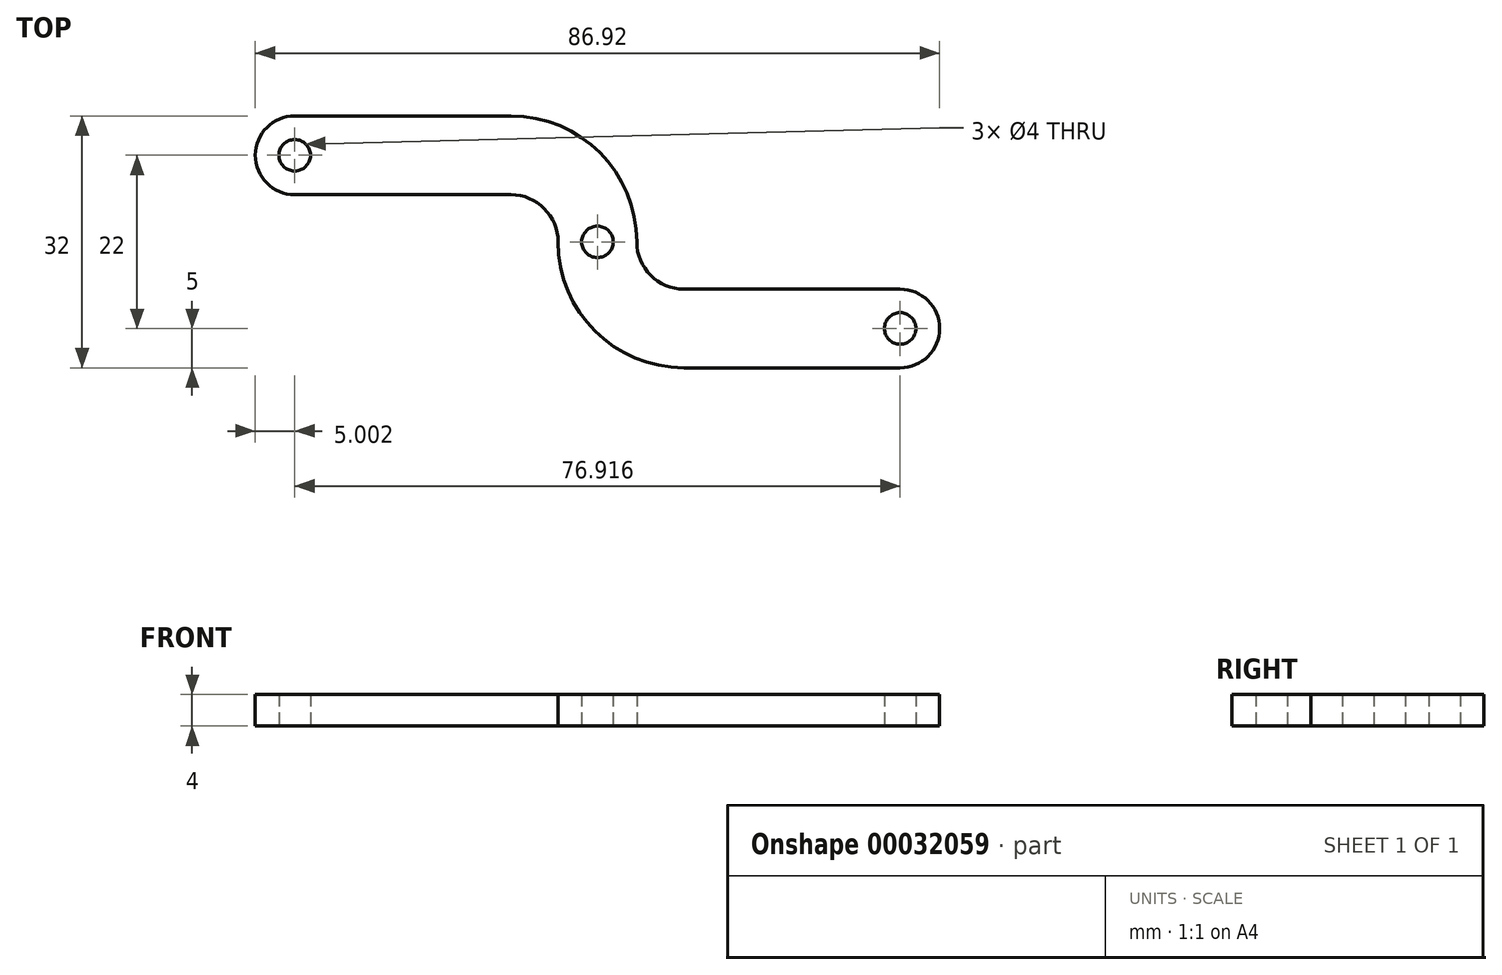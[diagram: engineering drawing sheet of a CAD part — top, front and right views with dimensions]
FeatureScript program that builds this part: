
annotation { "Feature Type Name" : "Feature", "Feature Type Description" : "" }
export const myFeature = defineFeature(function(context is Context, id is Id, definition is map)
    precondition{}
    {
        {
            var Q0;
            Q0=qCreatedBy(makeId("Top.planeOp"),FACE);
            var sketch = newSketch(context, id + "F0", { "sketchPlane" : qUnion([Q0])});
            skCircle(sketch, "E0", {"center": v(0, 0) * mm, "radius": 2 * mm});
            skCircle(sketch, "E1", {"center": v(-38.46, 11) * mm, "radius": 2 * mm});
            skCircle(sketch, "E2", {"center": v(38.46, -11) * mm, "radius": 2 * mm});
            skLineSegment(sketch, "E3", {"start": v(0, 16) * mm, "end": v(0, 6) * mm, "construction": true});
            skLineSegment(sketch, "E4", {"start": v(0, 6) * mm, "end": v(0, -6) * mm, "construction": true});
            skLineSegment(sketch, "E5", {"start": v(0, -6) * mm, "end": v(0, -16) * mm, "construction": true});
            skLineSegment(sketch, "E6", {"start": v(0, 11) * mm, "end": v(-38.46, 11) * mm, "construction": true});
            skLineSegment(sketch, "E7", {"start": v(0, -11) * mm, "end": v(38.46, -11) * mm, "construction": true});
            skCircle(sketch, "E8", {"center": v(0, 0) * mm, "radius": 5 * mm, "construction": true});
            skCircle(sketch, "E9", {"center": v(-38.46, 11) * mm, "radius": 5 * mm, "construction": true});
            skCircle(sketch, "E10", {"center": v(38.46, -11) * mm, "radius": 5 * mm, "construction": true});
            skArc(sketch, "E11", {"start": v(-5, 0) * mm, "mid": v(-6.76, 4.24) * mm, "end": v(-11, 6) * mm});
            skLineSegment(sketch, "E12", {"start": v(-38.46, 6) * mm, "end": v(-11, 6) * mm});
            skLineSegment(sketch, "E13", {"start": v(-38.46, 16) * mm, "end": v(-11, 16) * mm});
            skArc(sketch, "E14", {"start": v(5, 0) * mm, "mid": v(0.31, 11.31) * mm, "end": v(-11, 16) * mm});
            skArc(sketch, "E15", {"start": v(-38.46, 16) * mm, "mid": v(-43.46, 11) * mm, "end": v(-38.46, 6) * mm});
            skArc(sketch, "E16", {"start": v(-5, 0) * mm, "mid": v(-0.31, -11.31) * mm, "end": v(11, -16) * mm});
            skArc(sketch, "E17", {"start": v(5, 0) * mm, "mid": v(6.76, -4.24) * mm, "end": v(11, -6) * mm});
            skLineSegment(sketch, "E18", {"start": v(11, -6) * mm, "end": v(38.46, -6) * mm});
            skLineSegment(sketch, "E19", {"start": v(11, -16) * mm, "end": v(38.46, -16) * mm});
            skArc(sketch, "E20", {"start": v(38.46, -16) * mm, "mid": v(43.46, -11) * mm, "end": v(38.46, -6) * mm});
            skSolve(sketch);
        }
        {
            var Q0;
            Q0 = qSketchRegion(id + "F0", true);
            extrude(context, id + "F1", {"entities" : qUnion([Q0]), "depth" : 4 * mm});
        }
    });
